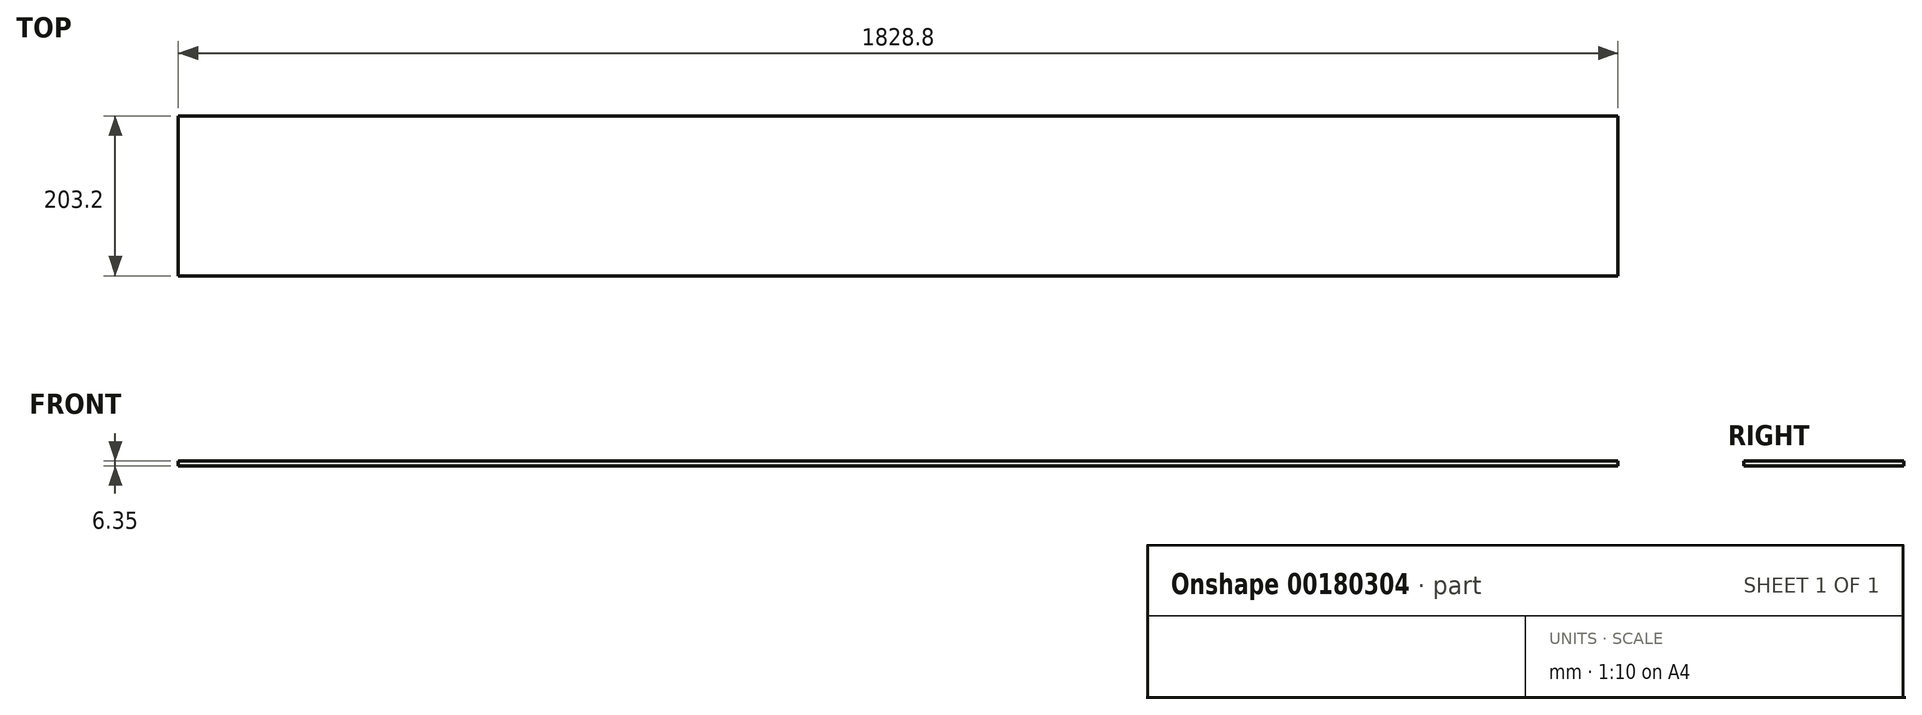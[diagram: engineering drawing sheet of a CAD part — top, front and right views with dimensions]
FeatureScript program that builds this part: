
annotation { "Feature Type Name" : "Feature", "Feature Type Description" : "" }
export const myFeature = defineFeature(function(context is Context, id is Id, definition is map)
    precondition{}
    {
        {
            var Q0;
            Q0=qCreatedBy(makeId("Top.planeOp"),FACE);
            var sketch = newSketch(context, id + "F0", { "sketchPlane" : qUnion([Q0])});
            skLineSegment(sketch, "E0.bottom", {"start": v(0, 0) * mm, "end": v(1828.8, 0) * mm});
            skLineSegment(sketch, "E0.top", {"start": v(0, 203.2) * mm, "end": v(1828.8, 203.2) * mm});
            skLineSegment(sketch, "E0.left", {"start": v(0, 0) * mm, "end": v(0, 203.2) * mm});
            skLineSegment(sketch, "E0.right", {"start": v(1828.8, 0) * mm, "end": v(1828.8, 203.2) * mm});
            skSolve(sketch);
        }
        {
            var Q0;
            Q0 = qSketchRegion(id + "F0", true);
            extrude(context, id + "F1", {"entities" : qUnion([Q0]), "depth" : 6.35 * mm});
        }
    });
